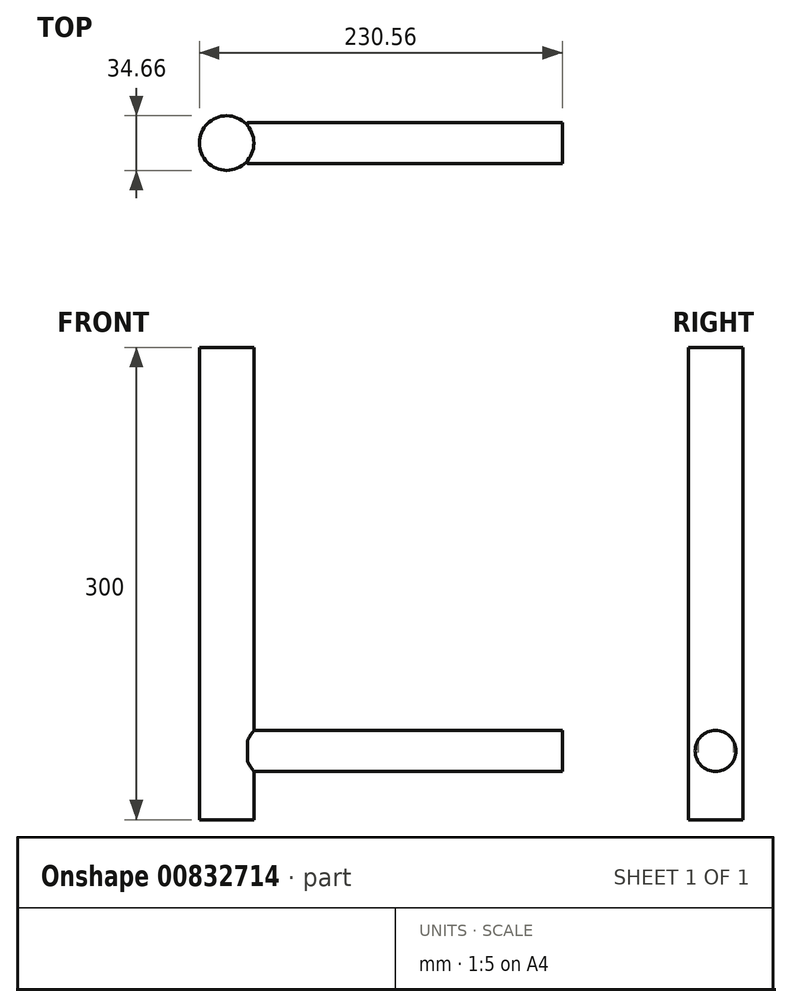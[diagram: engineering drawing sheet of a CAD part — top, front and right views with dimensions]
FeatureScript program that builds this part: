
annotation { "Feature Type Name" : "Feature", "Feature Type Description" : "" }
export const myFeature = defineFeature(function(context is Context, id is Id, definition is map)
    precondition{}
    {
        {
            var Q0;
            Q0=qCreatedBy(makeId("Top.planeOp"),FACE);
            var sketch = newSketch(context, id + "F0", { "sketchPlane" : qUnion([Q0])});
            skCircle(sketch, "E0", {"center": v(-54.53, 0) * mm, "radius": 17.33 * mm});
            skLineSegment(sketch, "E1", {"start": v(-29.34, 0) * mm, "end": v(22.18, 0) * mm});
            skSolve(sketch);
        }
        {
            var Q0;
            Q0=makeQuery(id+"F0.imprint","IMPRINT",FACE,{"disambiguationData":[TD([[makeQuery(id+"F0.imprint","IMPRINT",EDGE,{"derivedFrom":sQuery(id+"F0.wireOp",EDGE,"E0")}),1.0]])]});
            extrude(context, id + "F1", {"entities" : qUnion([Q0]), "depth" : 300 * mm, "offsetDistance" : 25 * mm});
        }
        {
            var Q0;
            Q0=qCreatedBy(makeId("Right.planeOp"),FACE);
            cPlane(context, id + "F2", {"entities" : qUnion([Q0]), "cplaneType" : CPlaneType.OFFSET, "offset" : 41.3 * mm, "oppositeDirection" : true, "width" : 150 * mm, "height" : 150 * mm});
        }
        {
            var Q0;
            Q0=qCreatedBy(id+"F2.planeOp",FACE);
            var sketch = newSketch(context, id + "F3", { "sketchPlane" : qUnion([Q0])});
            skCircle(sketch, "E2", {"center": v(0, 43.7) * mm, "radius": 13 * mm});
            skSolve(sketch);
        }
        {
            var Q0;
            Q0 = qSketchRegion(id + "F3", true);
            extrude(context, id + "F4", {"entities" : qUnion([Q0]), "operationType" : NewBodyOperationType.ADD, "depth" : 200 * mm, "offsetDistance" : 25 * mm});
        }
    });
